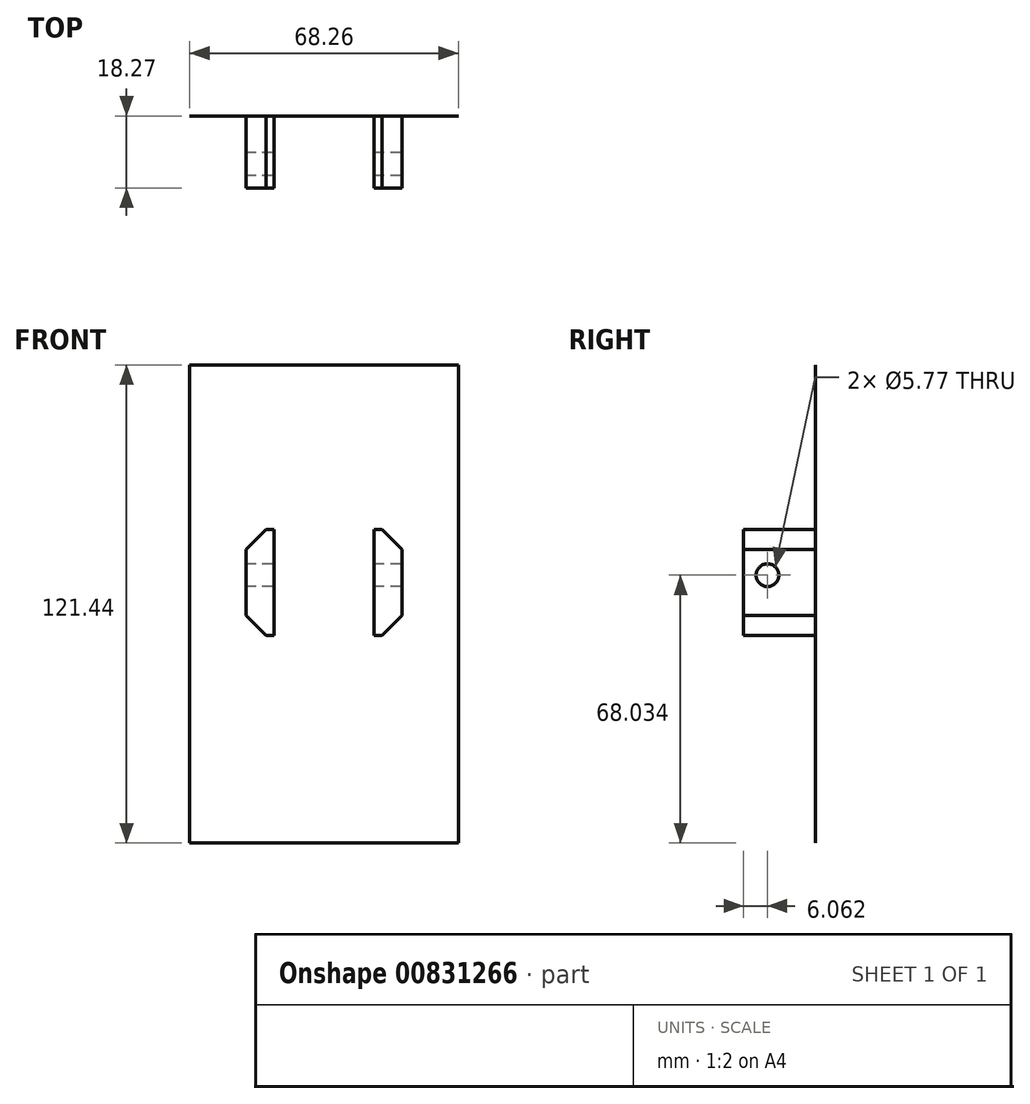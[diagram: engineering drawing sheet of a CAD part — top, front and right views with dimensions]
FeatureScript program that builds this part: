
annotation { "Feature Type Name" : "Feature", "Feature Type Description" : "" }
export const myFeature = defineFeature(function(context is Context, id is Id, definition is map)
    precondition{}
    {
        {
            var Q0;
            Q0=qCreatedBy(makeId("Front.planeOp"),FACE);
            var sketch = newSketch(context, id + "F0", { "sketchPlane" : qUnion([Q0])});
            skLineSegment(sketch, "E0", {"start": v(-34.13, 54.9) * mm, "end": v(34.13, 54.9) * mm});
            skLineSegment(sketch, "E1", {"start": v(-34.13, 54.9) * mm, "end": v(-34.13, -66.54) * mm});
            skLineSegment(sketch, "E2", {"start": v(-34.13, -66.54) * mm, "end": v(34.13, -66.54) * mm});
            skLineSegment(sketch, "E3", {"start": v(34.13, 54.9) * mm, "end": v(34.13, -66.54) * mm});
            skPoint(sketch, "E4", {"position": v(0, 54.9) * mm});
            skSolve(sketch);
        }
        {
            var Q0;
            Q0=qCreatedBy(makeId("Front.planeOp"),FACE);
            var sketch = newSketch(context, id + "F1", { "sketchPlane" : qUnion([Q0])});
            skLineSegment(sketch, "E5.bottom", {"start": v(12.7, 13.1) * mm, "end": v(19.84, 13.1) * mm});
            skLineSegment(sketch, "E5.top", {"start": v(12.7, -13.88) * mm, "end": v(19.84, -13.88) * mm});
            skLineSegment(sketch, "E5.left", {"start": v(12.7, 13.1) * mm, "end": v(12.7, -13.88) * mm});
            skLineSegment(sketch, "E5.right", {"start": v(19.84, 13.1) * mm, "end": v(19.84, -13.88) * mm});
            skLineSegment(sketch, "E6.bottom", {"start": v(-19.85, 13.1) * mm, "end": v(-12.7, 13.1) * mm});
            skLineSegment(sketch, "E6.top", {"start": v(-19.85, -13.88) * mm, "end": v(-12.7, -13.88) * mm});
            skLineSegment(sketch, "E6.left", {"start": v(-19.85, 13.1) * mm, "end": v(-19.85, -13.88) * mm});
            skLineSegment(sketch, "E6.right", {"start": v(-12.7, 13.1) * mm, "end": v(-12.7, -13.88) * mm});
            skSolve(sketch);
        }
        {
            var Q0;
            Q0 = qSketchRegion(id + "F1", true);
            extrude(context, id + "F2", {"entities" : qUnion([Q0]), "depth" : 18.26 * mm, "offsetDistance" : 25.4 * mm});
        }
        {
            var Q0;
            Q0=makeQuery(id+"F2.opExtrude","SWEPT_EDGE",EDGE,{"disambiguationData":[OSD([sQuery(id+"F1.wireOp",EDGE,"E6.bottom"),sQuery(id+"F1.wireOp",EDGE,"E6.left")])]});
            var Q1;
            Q1=makeQuery(id+"F2.opExtrude","SWEPT_EDGE",EDGE,{"disambiguationData":[OSD([sQuery(id+"F1.wireOp",EDGE,"E5.bottom"),sQuery(id+"F1.wireOp",EDGE,"E5.right")])]});
            var Q2;
            Q2=makeQuery(id+"F2.opExtrude","SWEPT_EDGE",EDGE,{"disambiguationData":[OSD([sQuery(id+"F1.wireOp",EDGE,"E5.top"),sQuery(id+"F1.wireOp",EDGE,"E5.right")])]});
            var Q3;
            Q3=makeQuery(id+"F2.opExtrude","SWEPT_EDGE",EDGE,{"disambiguationData":[OSD([sQuery(id+"F1.wireOp",EDGE,"E6.top"),sQuery(id+"F1.wireOp",EDGE,"E6.left")])]});
            chamfer(context, id + "F3", {"entities" : qUnion([Q0, Q1, Q2, Q3]), "width" : 5.08 * mm, "tangentPropagation" : true});
        }
        {
            var Q0;
            Q0=makeQuery(id+"F2.opExtrude","SWEPT_FACE",FACE,{"disambiguationData":[OSD([sQuery(id+"F1.wireOp",EDGE,"E6.left")])]});
            var sketch = newSketch(context, id + "F4", { "sketchPlane" : qUnion([Q0])});
            skCircle(sketch, "E7", {"center": v(12.2, 1.5) * mm, "radius": 2.88 * mm});
            skSolve(sketch);
        }
        {
            var Q0;
            Q0=makeQuery(id+"F4.imprint","IMPRINT",FACE,{"disambiguationData":[TD([[makeQuery(id+"F4.imprint","IMPRINT",EDGE,{"derivedFrom":sQuery(id+"F4.wireOp",EDGE,"E7")}),1.0]])]});
            var Q1;
            Q1=sQuery(id+"F4.wireOp",EDGE,"E7");
            extrude(context, id + "F5", {"entities" : qUnion([Q0]), "operationType" : NewBodyOperationType.REMOVE, "surfaceEntities" : qUnion([Q1]), "oppositeDirection" : true, "depth" : 50.8 * mm, "offsetDistance" : 25.4 * mm});
        }
        {
            var Q0;
            Q0 = qSketchRegion(id + "F0", true);
            extrude(context, id + "F6", {"entities" : qUnion([Q0]), "depth" : -1 / 101.6 * mm, "offsetDistance" : 25.4 * mm});
        }
    });
